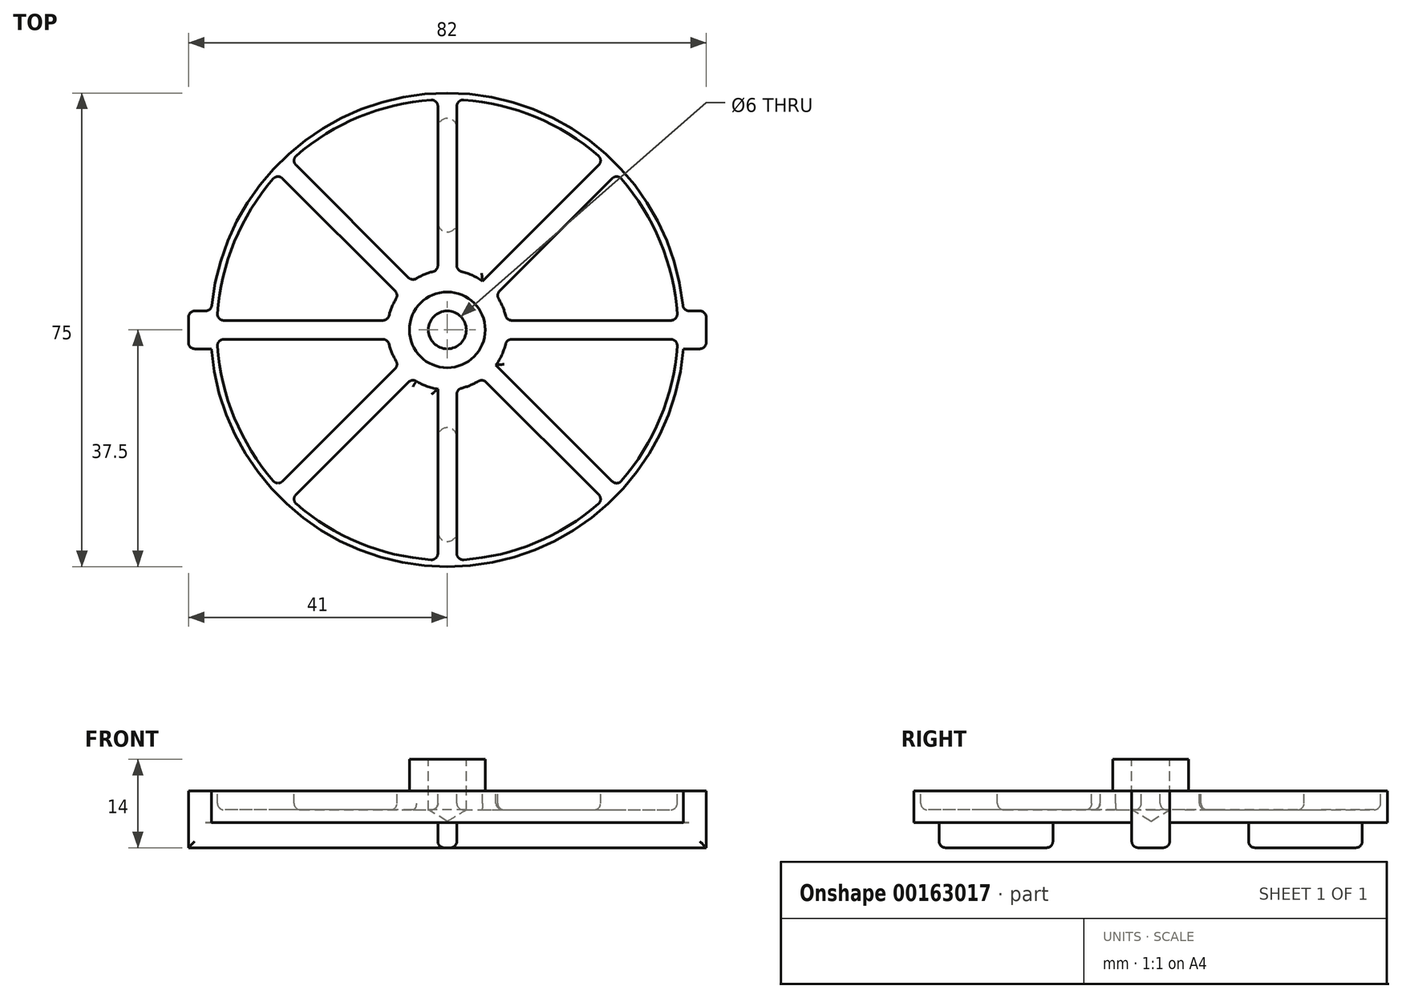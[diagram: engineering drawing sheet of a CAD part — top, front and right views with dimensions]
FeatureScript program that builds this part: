
annotation { "Feature Type Name" : "Feature", "Feature Type Description" : "" }
export const myFeature = defineFeature(function(context is Context, id is Id, definition is map)
    precondition{}
    {
        {
            var Q0;
            Q0=qCreatedBy(makeId("Top.planeOp"),FACE);
            var sketch = newSketch(context, id + "F0", { "sketchPlane" : qUnion([Q0])});
            skCircle(sketch, "E0", {"center": v(0, 0) * mm, "radius": 37.5 * mm});
            skSolve(sketch);
        }
        {
            var Q0;
            Q0 = qSketchRegion(id + "F0", true);
            extrude(context, id + "F1", {"entities" : qUnion([Q0]), "depth" : 5 * mm});
        }
        {
            var Q0;
            Q0=makeQuery(id+"F1.opExtrude","CAP_FACE",FACE,{"disambiguationData":[OSD([sQuery(id+"F0.wireOp",EDGE,"E0")])],"isStart":false});
            var sketch = newSketch(context, id + "F2", { "sketchPlane" : qUnion([Q0])});
            skArc(sketch, "E1", {"start": v(-27.56, 23.93) * mm, "mid": v(-33.72, 13.97) * mm, "end": v(-36.4, 2.57) * mm});
            skArc(sketch, "E2", {"start": v(9.23, 2.26) * mm, "mid": v(8.78, 3.64) * mm, "end": v(8.12, 4.92) * mm});
            skLineSegment(sketch, "E3", {"start": v(1.5, 10.2) * mm, "end": v(1.5, 35.41) * mm});
            skLineSegment(sketch, "E4.MirrorCS", {"start": v(-1.5, 10.2) * mm, "end": v(-1.5, 35.41) * mm});
            skLineSegment(sketch, "E5.1.0", {"start": v(-6.15, 8.27) * mm, "end": v(-23.98, 26.1) * mm});
            skLineSegment(sketch, "E5.1.1", {"start": v(-8.27, 6.15) * mm, "end": v(-26.1, 23.98) * mm});
            skLineSegment(sketch, "E5.2.0", {"start": v(-10.2, 1.5) * mm, "end": v(-35.41, 1.5) * mm});
            skLineSegment(sketch, "E5.2.1", {"start": v(-10.2, -1.5) * mm, "end": v(-35.41, -1.5) * mm});
            skLineSegment(sketch, "E5.3.0", {"start": v(-8.27, -6.15) * mm, "end": v(-26.1, -23.98) * mm});
            skLineSegment(sketch, "E5.3.1", {"start": v(-6.15, -8.27) * mm, "end": v(-23.98, -26.1) * mm});
            skLineSegment(sketch, "E5.4.0", {"start": v(-1.5, -9.38) * mm, "end": v(-1.5, -35.41) * mm});
            skLineSegment(sketch, "E5.4.1", {"start": v(1.5, -10.2) * mm, "end": v(1.5, -35.41) * mm});
            skLineSegment(sketch, "E5.5.0", {"start": v(6.15, -8.27) * mm, "end": v(23.98, -26.1) * mm});
            skLineSegment(sketch, "E5.5.1", {"start": v(7.7, -5.57) * mm, "end": v(26.1, -23.98) * mm});
            skLineSegment(sketch, "E5.6.0", {"start": v(10.2, -1.5) * mm, "end": v(35.41, -1.5) * mm});
            skLineSegment(sketch, "E5.6.1", {"start": v(10.2, 1.5) * mm, "end": v(35.41, 1.5) * mm});
            skLineSegment(sketch, "E5.7.0", {"start": v(8.27, 6.15) * mm, "end": v(26.1, 23.98) * mm});
            skLineSegment(sketch, "E5.7.1", {"start": v(5.57, 7.7) * mm, "end": v(23.98, 26.1) * mm});
            skArc(sketch, "E6.trimOffspring", {"start": v(-2.57, 36.4) * mm, "mid": v(-13.97, 33.72) * mm, "end": v(-23.93, 27.56) * mm});
            skArc(sketch, "E7.trimOffspring", {"start": v(23.93, 27.56) * mm, "mid": v(13.97, 33.72) * mm, "end": v(2.57, 36.4) * mm});
            skArc(sketch, "E8.trimOffspring", {"start": v(36.4, 2.57) * mm, "mid": v(33.72, 13.97) * mm, "end": v(27.56, 23.93) * mm});
            skArc(sketch, "E9.trimOffspring", {"start": v(5.57, 7.7) * mm, "mid": v(4, 8.62) * mm, "end": v(2.26, 9.23) * mm});
            skArc(sketch, "E10.trimOffspring", {"start": v(-2.26, 9.23) * mm, "mid": v(-3.64, 8.78) * mm, "end": v(-4.92, 8.12) * mm});
            skArc(sketch, "E11.trimOffspring", {"start": v(-8.12, 4.92) * mm, "mid": v(-8.78, 3.64) * mm, "end": v(-9.23, 2.26) * mm});
            skArc(sketch, "E12.trimOffspring", {"start": v(-9.23, -2.26) * mm, "mid": v(-8.78, -3.64) * mm, "end": v(-8.12, -4.92) * mm});
            skArc(sketch, "E13.trimOffspring", {"start": v(-4.92, -8.12) * mm, "mid": v(-3.27, -8.92) * mm, "end": v(-1.5, -9.38) * mm});
            skArc(sketch, "E14.trimOffspring", {"start": v(2.26, -9.23) * mm, "mid": v(3.64, -8.78) * mm, "end": v(4.92, -8.12) * mm});
            skArc(sketch, "E15.trimOffspring", {"start": v(7.7, -5.57) * mm, "mid": v(8.62, -4) * mm, "end": v(9.23, -2.26) * mm});
            skArc(sketch, "E16.trimOffspring", {"start": v(27.56, -23.93) * mm, "mid": v(33.72, -13.97) * mm, "end": v(36.4, -2.57) * mm});
            skArc(sketch, "E17.trimOffspring", {"start": v(2.57, -36.4) * mm, "mid": v(13.97, -33.72) * mm, "end": v(23.93, -27.56) * mm});
            skArc(sketch, "E18.trimOffspring", {"start": v(-23.93, -27.56) * mm, "mid": v(-13.97, -33.72) * mm, "end": v(-2.57, -36.4) * mm});
            skArc(sketch, "E19.trimOffspring", {"start": v(-36.4, -2.57) * mm, "mid": v(-33.72, -13.97) * mm, "end": v(-27.56, -23.93) * mm});
            skPoint(sketch, "E20.visualSharp", {"position": v(1.5, 36.47) * mm});
            skArc(sketch, "E20.filletArc", {"start": v(2.57, 36.4) * mm, "mid": v(1.82, 36.14) * mm, "end": v(1.5, 35.41) * mm});
            skPoint(sketch, "E21.visualSharp", {"position": v(-1.5, 36.47) * mm});
            skArc(sketch, "E21.filletArc", {"start": v(-1.5, 35.41) * mm, "mid": v(-1.82, 36.14) * mm, "end": v(-2.57, 36.4) * mm});
            skPoint(sketch, "E22.visualSharp", {"position": v(24.73, 26.85) * mm});
            skArc(sketch, "E22.filletArc", {"start": v(23.98, 26.1) * mm, "mid": v(24.27, 26.84) * mm, "end": v(23.93, 27.56) * mm});
            skPoint(sketch, "E23.visualSharp", {"position": v(26.85, 24.73) * mm});
            skArc(sketch, "E23.filletArc", {"start": v(27.56, 23.93) * mm, "mid": v(26.84, 24.27) * mm, "end": v(26.1, 23.98) * mm});
            skPoint(sketch, "E24.visualSharp", {"position": v(-24.73, 26.85) * mm});
            skArc(sketch, "E24.filletArc", {"start": v(-23.93, 27.56) * mm, "mid": v(-24.27, 26.84) * mm, "end": v(-23.98, 26.1) * mm});
            skPoint(sketch, "E25.visualSharp", {"position": v(-26.85, 24.73) * mm});
            skArc(sketch, "E25.filletArc", {"start": v(-26.1, 23.98) * mm, "mid": v(-26.84, 24.27) * mm, "end": v(-27.56, 23.93) * mm});
            skPoint(sketch, "E26.visualSharp", {"position": v(-36.47, 1.5) * mm});
            skArc(sketch, "E26.filletArc", {"start": v(-36.4, 2.57) * mm, "mid": v(-36.14, 1.82) * mm, "end": v(-35.41, 1.5) * mm});
            skPoint(sketch, "E27.visualSharp", {"position": v(-36.47, -1.5) * mm});
            skArc(sketch, "E27.filletArc", {"start": v(-35.41, -1.5) * mm, "mid": v(-36.14, -1.82) * mm, "end": v(-36.4, -2.57) * mm});
            skPoint(sketch, "E28.visualSharp", {"position": v(36.47, 1.5) * mm});
            skArc(sketch, "E28.filletArc", {"start": v(35.41, 1.5) * mm, "mid": v(36.14, 1.82) * mm, "end": v(36.4, 2.57) * mm});
            skPoint(sketch, "E29.visualSharp", {"position": v(36.47, -1.5) * mm});
            skArc(sketch, "E29.filletArc", {"start": v(36.4, -2.57) * mm, "mid": v(36.14, -1.82) * mm, "end": v(35.41, -1.5) * mm});
            skPoint(sketch, "E30.visualSharp", {"position": v(26.85, -24.73) * mm});
            skArc(sketch, "E30.filletArc", {"start": v(26.1, -23.98) * mm, "mid": v(26.84, -24.27) * mm, "end": v(27.56, -23.93) * mm});
            skPoint(sketch, "E31.visualSharp", {"position": v(24.73, -26.85) * mm});
            skArc(sketch, "E31.filletArc", {"start": v(23.93, -27.56) * mm, "mid": v(24.27, -26.84) * mm, "end": v(23.98, -26.1) * mm});
            skPoint(sketch, "E32.visualSharp", {"position": v(1.5, -36.47) * mm});
            skArc(sketch, "E32.filletArc", {"start": v(1.5, -35.41) * mm, "mid": v(1.82, -36.14) * mm, "end": v(2.57, -36.4) * mm});
            skPoint(sketch, "E33.visualSharp", {"position": v(-1.5, -36.47) * mm});
            skArc(sketch, "E33.filletArc", {"start": v(-2.57, -36.4) * mm, "mid": v(-1.82, -36.14) * mm, "end": v(-1.5, -35.41) * mm});
            skPoint(sketch, "E34.visualSharp", {"position": v(-24.73, -26.85) * mm});
            skArc(sketch, "E34.filletArc", {"start": v(-23.98, -26.1) * mm, "mid": v(-24.27, -26.84) * mm, "end": v(-23.93, -27.56) * mm});
            skPoint(sketch, "E35.visualSharp", {"position": v(-26.85, -24.73) * mm});
            skArc(sketch, "E35.filletArc", {"start": v(-27.56, -23.93) * mm, "mid": v(-26.84, -24.27) * mm, "end": v(-26.1, -23.98) * mm});
            skPoint(sketch, "E36.visualSharp", {"position": v(-1.5, 9.38) * mm});
            skArc(sketch, "E36.filletArc", {"start": v(-2.26, 9.23) * mm, "mid": v(-1.71, 9.58) * mm, "end": v(-1.5, 10.2) * mm});
            skPoint(sketch, "E37.visualSharp", {"position": v(-5.57, 7.7) * mm});
            skArc(sketch, "E37.filletArc", {"start": v(-6.15, 8.27) * mm, "mid": v(-5.56, 7.99) * mm, "end": v(-4.92, 8.12) * mm});
            skPoint(sketch, "E38.visualSharp", {"position": v(-7.7, 5.57) * mm});
            skArc(sketch, "E38.filletArc", {"start": v(-8.12, 4.92) * mm, "mid": v(-7.99, 5.56) * mm, "end": v(-8.27, 6.15) * mm});
            skPoint(sketch, "E39.visualSharp", {"position": v(-9.38, -1.5) * mm});
            skArc(sketch, "E39.filletArc", {"start": v(-9.23, -2.26) * mm, "mid": v(-9.58, -1.71) * mm, "end": v(-10.2, -1.5) * mm});
            skPoint(sketch, "E40.visualSharp", {"position": v(-7.7, -5.57) * mm});
            skArc(sketch, "E40.filletArc", {"start": v(-8.27, -6.15) * mm, "mid": v(-7.99, -5.56) * mm, "end": v(-8.12, -4.92) * mm});
            skPoint(sketch, "E41.visualSharp", {"position": v(-9.38, 1.5) * mm});
            skArc(sketch, "E41.filletArc", {"start": v(-10.2, 1.5) * mm, "mid": v(-9.58, 1.71) * mm, "end": v(-9.23, 2.26) * mm});
            skPoint(sketch, "E42.visualSharp", {"position": v(-5.57, -7.7) * mm});
            skArc(sketch, "E42.filletArc", {"start": v(-4.92, -8.12) * mm, "mid": v(-5.56, -7.99) * mm, "end": v(-6.15, -8.27) * mm});
            skPoint(sketch, "E43.visualSharp", {"position": v(1.5, -9.38) * mm});
            skArc(sketch, "E43.filletArc", {"start": v(2.26, -9.23) * mm, "mid": v(1.71, -9.58) * mm, "end": v(1.5, -10.2) * mm});
            skPoint(sketch, "E44.visualSharp", {"position": v(5.57, -7.7) * mm});
            skArc(sketch, "E44.filletArc", {"start": v(6.15, -8.27) * mm, "mid": v(5.56, -7.99) * mm, "end": v(4.92, -8.12) * mm});
            skPoint(sketch, "E45.visualSharp", {"position": v(9.38, -1.5) * mm});
            skArc(sketch, "E45.filletArc", {"start": v(10.2, -1.5) * mm, "mid": v(9.58, -1.71) * mm, "end": v(9.23, -2.26) * mm});
            skPoint(sketch, "E46.visualSharp", {"position": v(9.38, 1.5) * mm});
            skArc(sketch, "E46.filletArc", {"start": v(9.23, 2.26) * mm, "mid": v(9.58, 1.71) * mm, "end": v(10.2, 1.5) * mm});
            skPoint(sketch, "E47.visualSharp", {"position": v(7.7, 5.57) * mm});
            skArc(sketch, "E47.filletArc", {"start": v(8.27, 6.15) * mm, "mid": v(7.99, 5.56) * mm, "end": v(8.12, 4.92) * mm});
            skPoint(sketch, "E48.visualSharp", {"position": v(1.5, 9.38) * mm});
            skArc(sketch, "E48.filletArc", {"start": v(1.5, 10.2) * mm, "mid": v(1.71, 9.58) * mm, "end": v(2.26, 9.23) * mm});
            skSolve(sketch);
        }
        {
            var Q0;
            Q0 = qSketchRegion(id + "F2", true);
            extrude(context, id + "F3", {"entities" : qUnion([Q0]), "operationType" : NewBodyOperationType.REMOVE, "oppositeDirection" : true, "depth" : 3 * mm});
        }
        {
            var Q0;
            Q0=makeQuery(id+"F1.opExtrude","CAP_FACE",FACE,{"disambiguationData":[OSD([sQuery(id+"F0.wireOp",EDGE,"E0")])],"isStart":true});
            var sketch = newSketch(context, id + "F4", { "sketchPlane" : qUnion([Q0])});
            skLineSegment(sketch, "E49.bottom", {"start": v(41, 3) * mm, "end": v(-41, 3) * mm});
            skLineSegment(sketch, "E49.top", {"start": v(41, -3) * mm, "end": v(-41, -3) * mm});
            skLineSegment(sketch, "E49.left", {"start": v(41, 3) * mm, "end": v(41, -3) * mm});
            skLineSegment(sketch, "E49.right", {"start": v(-41, 3) * mm, "end": v(-41, -3) * mm});
            skPoint(sketch, "E49.middle", {"position": v(0, 0) * mm});
            skSolve(sketch);
        }
        {
            var Q0;
            Q0 = qSketchRegion(id + "F4", true);
            extrude(context, id + "F5", {"entities" : qUnion([Q0]), "operationType" : NewBodyOperationType.ADD, "depth" : 4 * mm});
        }
        {
            var Q0;
            {var subQ0=sQuery(id+"F4.wireOp",EDGE,"E49.top");var subQ1=sQuery(id+"F4.wireOp",EDGE,"E49.bottom");var subQ3=sQuery(id+"F4.wireOp",EDGE,"E49.right");Q0=makeQuery(id+"F5.boolean.opBoolean","SPLIT",FACE,{"disambiguationData":[TD([makeQuery(id+"F5.opExtrude","SWEPT_FACE",FACE,{"disambiguationData":[OSD([subQ3])]})])],"derivedFrom":makeQuery(id+"F5.opExtrude","CAP_FACE",FACE,{"disambiguationData":[OSD([subQ1,subQ0,sQuery(id+"F4.wireOp",EDGE,"E49.left"),subQ3])],"isStart":true})});}
            var sketch = newSketch(context, id + "F6", { "sketchPlane" : qUnion([Q0])});
            skLineSegment(sketch, "E50", {"start": v(-41, 3) * mm, "end": v(-41, -3) * mm});
            skLineSegment(sketch, "E51", {"start": v(-41, -3) * mm, "end": v(-37.38, -3) * mm});
            skArc(sketch, "E52", {"start": v(-37.38, 3) * mm, "mid": v(-37.48, 0) * mm, "end": v(-37.38, -3) * mm});
            skLineSegment(sketch, "E53", {"start": v(-37.38, 3) * mm, "end": v(-41, 3) * mm});
            skLineSegment(sketch, "E54", {"start": v(0, -3.25) * mm, "end": v(0, 3.49) * mm, "construction": true});
            skLineSegment(sketch, "E55.MirrorCS", {"start": v(41, -3) * mm, "end": v(37.38, -3) * mm});
            skLineSegment(sketch, "E56.MirrorCS", {"start": v(41, 3) * mm, "end": v(41, -3) * mm});
            skLineSegment(sketch, "E57.MirrorCS", {"start": v(37.38, 3) * mm, "end": v(41, 3) * mm});
            skArc(sketch, "E58.MirrorCS", {"start": v(37.38, 3) * mm, "mid": v(37.48, 0) * mm, "end": v(37.38, -3) * mm});
            skSolve(sketch);
        }
        {
            var Q0;
            Q0 = qSketchRegion(id + "F6", true);
            var Q1;
            Q1=makeQuery(id+"F1.opExtrude","CAP_FACE",FACE,{"disambiguationData":[OSD([sQuery(id+"F0.wireOp",EDGE,"E0")])],"isStart":false});
            extrude(context, id + "F7", {"entities" : qUnion([Q0]), "operationType" : NewBodyOperationType.ADD, "endBound" : BoundingType.UP_TO_SURFACE, "endBoundEntityFace" : qUnion([Q1]), "depth" : 25 * mm});
        }
        {
            var Q0;
            Q0=makeQuery(id+"F7.boolean.opBoolean","MERGE",EDGE,{"derivedFrom":[makeQuery(id+"F5.opExtrude","SWEPT_EDGE",EDGE,{"disambiguationData":[OSD([sQuery(id+"F4.wireOp",EDGE,"E49.top"),sQuery(id+"F4.wireOp",EDGE,"E49.right")])]}),makeQuery(id+"F7.opExtrude","SWEPT_EDGE",EDGE,{"disambiguationData":[OSD([sQuery(id+"F6.wireOp",EDGE,"E50"),sQuery(id+"F6.wireOp",EDGE,"E53")])]})]});
            var Q1;
            Q1=makeQuery(id+"F7.boolean.opBoolean","MERGE",EDGE,{"derivedFrom":[makeQuery(id+"F5.opExtrude","SWEPT_EDGE",EDGE,{"disambiguationData":[OSD([sQuery(id+"F4.wireOp",EDGE,"E49.bottom"),sQuery(id+"F4.wireOp",EDGE,"E49.right")])]}),makeQuery(id+"F7.opExtrude","SWEPT_EDGE",EDGE,{"disambiguationData":[OSD([sQuery(id+"F6.wireOp",EDGE,"E50"),sQuery(id+"F6.wireOp",EDGE,"E51")])]})]});
            var Q2;
            Q2=makeQuery(id+"F7.boolean.opBoolean","MERGE",EDGE,{"derivedFrom":[makeQuery(id+"F5.opExtrude","SWEPT_EDGE",EDGE,{"disambiguationData":[OSD([sQuery(id+"F4.wireOp",EDGE,"E49.bottom"),sQuery(id+"F4.wireOp",EDGE,"E49.left")])]}),makeQuery(id+"F7.opExtrude","SWEPT_EDGE",EDGE,{"disambiguationData":[OSD([sQuery(id+"F6.wireOp",EDGE,"E55.MirrorCS"),sQuery(id+"F6.wireOp",EDGE,"E56.MirrorCS")])]})]});
            var Q3;
            Q3=makeQuery(id+"F7.boolean.opBoolean","MERGE",EDGE,{"derivedFrom":[makeQuery(id+"F5.opExtrude","SWEPT_EDGE",EDGE,{"disambiguationData":[OSD([sQuery(id+"F4.wireOp",EDGE,"E49.top"),sQuery(id+"F4.wireOp",EDGE,"E49.left")])]}),makeQuery(id+"F7.opExtrude","SWEPT_EDGE",EDGE,{"disambiguationData":[OSD([sQuery(id+"F6.wireOp",EDGE,"E56.MirrorCS"),sQuery(id+"F6.wireOp",EDGE,"E57.MirrorCS")])]})]});
            var Q4;
            Q4=makeQuery(id+"F5.opExtrude","CAP_EDGE",EDGE,{"disambiguationData":[OSD([sQuery(id+"F4.wireOp",EDGE,"E49.top")])],"isStart":false});
            var Q5;
            Q5=makeQuery(id+"F5.opExtrude","CAP_EDGE",EDGE,{"disambiguationData":[OSD([sQuery(id+"F4.wireOp",EDGE,"E49.bottom")])],"isStart":false});
            var Q6;
            {var subQ0=sQuery(id+"F0.wireOp",EDGE,"E0");var subQ1=sQuery(id+"F4.wireOp",EDGE,"E49.top");Q6=makeQuery(id+"F5.boolean.opBoolean","SPLIT",EDGE,{"disambiguationData":[TD([makeQuery(id+"F1.opExtrude","SWEPT_FACE",FACE,{"disambiguationData":[OSD([subQ0])]}),makeQuery(id+"F1.opExtrude","CAP_FACE",FACE,{"disambiguationData":[OSD([subQ0])],"isStart":true}),makeQuery(id+"F5.opExtrude","CAP_FACE",FACE,{"disambiguationData":[OSD([sQuery(id+"F4.wireOp",EDGE,"E49.bottom"),subQ1,sQuery(id+"F4.wireOp",EDGE,"E49.left"),sQuery(id+"F4.wireOp",EDGE,"E49.right")])],"isStart":true}),makeQuery(id+"F5.opExtrude","SWEPT_FACE",FACE,{"disambiguationData":[OSD([subQ1])]})])],"derivedFrom":makeQuery(id+"F5.opExtrude","CAP_EDGE",EDGE,{"disambiguationData":[OSD([subQ1])],"isStart":true})});}
            var Q7;
            {var subQ0=sQuery(id+"F0.wireOp",EDGE,"E0");var subQ1=sQuery(id+"F4.wireOp",EDGE,"E49.bottom");Q7=makeQuery(id+"F5.boolean.opBoolean","SPLIT",EDGE,{"disambiguationData":[TD([makeQuery(id+"F1.opExtrude","SWEPT_FACE",FACE,{"disambiguationData":[OSD([subQ0])]}),makeQuery(id+"F1.opExtrude","CAP_FACE",FACE,{"disambiguationData":[OSD([subQ0])],"isStart":true}),makeQuery(id+"F5.opExtrude","SWEPT_FACE",FACE,{"disambiguationData":[OSD([subQ1])]}),makeQuery(id+"F5.opExtrude","CAP_FACE",FACE,{"disambiguationData":[OSD([subQ1,sQuery(id+"F4.wireOp",EDGE,"E49.top"),sQuery(id+"F4.wireOp",EDGE,"E49.left"),sQuery(id+"F4.wireOp",EDGE,"E49.right")])],"isStart":true})])],"derivedFrom":makeQuery(id+"F5.opExtrude","CAP_EDGE",EDGE,{"disambiguationData":[OSD([subQ1])],"isStart":true})});}
            var Q8;
            Q8=makeQuery(id+"F7.opExtrude","SWEPT_EDGE",EDGE,{"disambiguationData":[OSD([sQuery(id+"F0.wireOp",EDGE,"E0"),sQuery(id+"F6.wireOp",EDGE,"E51"),sQuery(id+"F6.wireOp",EDGE,"E52")])]});
            var Q9;
            Q9=makeQuery(id+"F7.opExtrude","SWEPT_EDGE",EDGE,{"disambiguationData":[OSD([sQuery(id+"F0.wireOp",EDGE,"E0"),sQuery(id+"F6.wireOp",EDGE,"E52"),sQuery(id+"F6.wireOp",EDGE,"E53")])]});
            var Q10;
            Q10=makeQuery(id+"F7.opExtrude","SWEPT_EDGE",EDGE,{"disambiguationData":[OSD([sQuery(id+"F6.wireOp",EDGE,"E57.MirrorCS"),sQuery(id+"F6.wireOp",EDGE,"E58.MirrorCS")])]});
            var Q11;
            Q11=makeQuery(id+"F7.opExtrude","SWEPT_EDGE",EDGE,{"disambiguationData":[OSD([sQuery(id+"F6.wireOp",EDGE,"E55.MirrorCS"),sQuery(id+"F6.wireOp",EDGE,"E58.MirrorCS")])]});
            fillet(context, id + "F8", {"entities" : qUnion([Q0, Q1, Q2, Q3, Q4, Q5, Q6, Q7, Q8, Q9, Q10, Q11]), "radius" : 1 * mm, "tangentPropagation" : true, "allowEdgeOverflow" : false});
        }
        {
            var Q0;
            {var subQ0=sQuery(id+"F0.wireOp",EDGE,"E0");var subQ1=sQuery(id+"F4.wireOp",EDGE,"E49.bottom");Q0=makeQuery(id+"F5.boolean.opBoolean","SPLIT",FACE,{"disambiguationData":[TD([makeQuery(id+"F5.opExtrude","SWEPT_FACE",FACE,{"disambiguationData":[OSD([subQ1])]})])],"derivedFrom":makeQuery(id+"F1.opExtrude","CAP_FACE",FACE,{"disambiguationData":[OSD([subQ0])],"isStart":true})});}
            var sketch = newSketch(context, id + "F9", { "sketchPlane" : qUnion([Q0])});
            skPoint(sketch, "E59.startSnap0", {"position": v(0, 37.5) * mm});
            skLineSegment(sketch, "E60", {"start": v(0, 0) * mm, "end": v(5.23, 0) * mm, "construction": true});
            skArc(sketch, "E61.0.startCap", {"start": v(-1.5, 32) * mm, "mid": v(0, 33.5) * mm, "end": v(1.5, 32) * mm});
            skArc(sketch, "E61.0.endCap", {"start": v(1.5, 17) * mm, "mid": v(0, 15.5) * mm, "end": v(-1.5, 17) * mm});
            skLineSegment(sketch, "E61.0.left", {"start": v(1.5, 32) * mm, "end": v(1.5, 17) * mm});
            skLineSegment(sketch, "E61.0.right", {"start": v(-1.5, 32) * mm, "end": v(-1.5, 17) * mm});
            skArc(sketch, "E62.MirrorCS", {"start": v(-1.5, -32) * mm, "mid": v(0, -33.5) * mm, "end": v(1.5, -32) * mm});
            skLineSegment(sketch, "E63.MirrorCS", {"start": v(1.5, -32) * mm, "end": v(1.5, -17) * mm});
            skLineSegment(sketch, "E64.MirrorCS", {"start": v(-1.5, -32) * mm, "end": v(-1.5, -17) * mm});
            skArc(sketch, "E65.MirrorCS", {"start": v(1.5, -17) * mm, "mid": v(0, -15.5) * mm, "end": v(-1.5, -17) * mm});
            skSolve(sketch);
        }
        {
            var Q0;
            Q0 = qSketchRegion(id + "F9", true);
            extrude(context, id + "F10", {"entities" : qUnion([Q0]), "operationType" : NewBodyOperationType.ADD, "depth" : 4 * mm});
        }
        {
            var Q0;
            Q0=makeQuery(id+"F10.opExtrude","CAP_EDGE",EDGE,{"disambiguationData":[OSD([sQuery(id+"F9.wireOp",EDGE,"E61.0.left")])],"isStart":false});
            var Q1;
            Q1=makeQuery(id+"F10.opExtrude","CAP_EDGE",EDGE,{"disambiguationData":[OSD([sQuery(id+"F9.wireOp",EDGE,"E61.0.right")])],"isStart":false});
            var Q2;
            Q2=makeQuery(id+"F10.opExtrude","CAP_FACE",FACE,{"disambiguationData":[OSD([sQuery(id+"F9.wireOp",EDGE,"E62.MirrorCS"),sQuery(id+"F9.wireOp",EDGE,"E63.MirrorCS"),sQuery(id+"F9.wireOp",EDGE,"E64.MirrorCS"),sQuery(id+"F9.wireOp",EDGE,"E65.MirrorCS")])],"isStart":false});
            var Q3;
            Q3=makeQuery(id+"F10.opExtrude","CAP_EDGE",EDGE,{"disambiguationData":[OSD([sQuery(id+"F9.wireOp",EDGE,"E63.MirrorCS")])],"isStart":false});
            fillet(context, id + "F11", {"entities" : qUnion([Q0, Q1, Q2, Q3]), "radius" : 1 * mm, "tangentPropagation" : true, "allowEdgeOverflow" : false});
        }
        {
            var Q0;
            {var subQ0=sQuery(id+"F0.wireOp",EDGE,"E0");Q0=makeQuery(id+"F7.boolean.opBoolean","MERGE",FACE,{"derivedFrom":[makeQuery(id+"F1.opExtrude","CAP_FACE",FACE,{"disambiguationData":[OSD([subQ0])],"isStart":false}),makeQuery(id+"F7.opExtrude","CAP_FACE",FACE,{"disambiguationData":[OSD([subQ0]),ownerDisambiguation([makeQuery(id+"F7.opExtrude","SWEPT_BODY",BODY,{"disambiguationData":[OSD([sQuery(id+"F6.wireOp",EDGE,"E50"),sQuery(id+"F6.wireOp",EDGE,"E51"),sQuery(id+"F6.wireOp",EDGE,"E52"),sQuery(id+"F6.wireOp",EDGE,"E53")])]})])],"isStart":false}),makeQuery(id+"F7.opExtrude","CAP_FACE",FACE,{"disambiguationData":[OSD([subQ0]),ownerDisambiguation([makeQuery(id+"F7.opExtrude","SWEPT_BODY",BODY,{"disambiguationData":[OSD([sQuery(id+"F6.wireOp",EDGE,"E55.MirrorCS"),sQuery(id+"F6.wireOp",EDGE,"E56.MirrorCS"),sQuery(id+"F6.wireOp",EDGE,"E57.MirrorCS"),sQuery(id+"F6.wireOp",EDGE,"E58.MirrorCS")])]})])],"isStart":false})]});}
            var sketch = newSketch(context, id + "F12", { "sketchPlane" : qUnion([Q0])});
            skCircle(sketch, "E66", {"center": v(0, 0) * mm, "radius": 6 * mm});
            skSolve(sketch);
        }
        {
            var Q0;
            Q0 = qSketchRegion(id + "F12", true);
            extrude(context, id + "F13", {"entities" : qUnion([Q0]), "operationType" : NewBodyOperationType.ADD, "depth" : 5 * mm});
        }
        {
            var Q0;
            Q0=makeQuery(id+"F13.opExtrude","CAP_FACE",FACE,{"disambiguationData":[OSD([sQuery(id+"F12.wireOp",EDGE,"E66")])],"isStart":false});
            var sketch = newSketch(context, id + "F14", { "sketchPlane" : qUnion([Q0])});
            skPoint(sketch, "E67", {"position": v(0, 0) * mm});
            skSolve(sketch);
        }
        {
            var Q0;
            Q0=sQuery(id+"F14.wireOp",VERTEX,"E67");
            var Q1;
            Q1=makeQuery(id+"F1.opExtrude","SWEPT_BODY",BODY,{"disambiguationData":[OSD([sQuery(id+"F0.wireOp",EDGE,"E0")])]});
            hole(context, id + "F15", {"style" : HoleStyle.SIMPLE, "endStyle" : HoleEndStyle.BLIND, "holeDiameter" : 6 * mm, "holeDepth" : 8 * mm, "locations" : qUnion([Q0]), "scope" : qUnion([Q1])});
        }
        {
            var Q0;
            Q0=makeQuery(id+"F3.boolean.opBoolean","COPY",EDGE,{"derivedFrom":makeQuery(id+"F3.opExtrude","CAP_EDGE",EDGE,{"disambiguationData":[OSD([sQuery(id+"F2.wireOp",EDGE,"E5.2.1")])],"isStart":false})});
            var Q1;
            Q1=makeQuery(id+"F3.boolean.opBoolean","COPY",EDGE,{"derivedFrom":makeQuery(id+"F3.opExtrude","CAP_EDGE",EDGE,{"disambiguationData":[OSD([sQuery(id+"F2.wireOp",EDGE,"E1")])],"isStart":false})});
            var Q2;
            Q2=makeQuery(id+"F3.boolean.opBoolean","COPY",EDGE,{"derivedFrom":makeQuery(id+"F3.opExtrude","CAP_EDGE",EDGE,{"disambiguationData":[OSD([sQuery(id+"F2.wireOp",EDGE,"E6.trimOffspring")])],"isStart":false})});
            var Q3;
            Q3=makeQuery(id+"F3.boolean.opBoolean","COPY",EDGE,{"derivedFrom":makeQuery(id+"F3.opExtrude","CAP_EDGE",EDGE,{"disambiguationData":[OSD([sQuery(id+"F2.wireOp",EDGE,"E3")])],"isStart":false})});
            var Q4;
            Q4=makeQuery(id+"F3.boolean.opBoolean","COPY",EDGE,{"derivedFrom":makeQuery(id+"F3.opExtrude","CAP_EDGE",EDGE,{"disambiguationData":[OSD([sQuery(id+"F2.wireOp",EDGE,"E5.7.0")])],"isStart":false})});
            var Q5;
            Q5=makeQuery(id+"F3.boolean.opBoolean","COPY",EDGE,{"derivedFrom":makeQuery(id+"F3.opExtrude","CAP_EDGE",EDGE,{"disambiguationData":[OSD([sQuery(id+"F2.wireOp",EDGE,"E7.trimOffspring")])],"isStart":false})});
            var Q6;
            Q6=makeQuery(id+"F3.boolean.opBoolean","COPY",EDGE,{"derivedFrom":makeQuery(id+"F3.opExtrude","CAP_EDGE",EDGE,{"disambiguationData":[OSD([sQuery(id+"F2.wireOp",EDGE,"E20.filletArc")])],"isStart":false})});
            var Q7;
            Q7=makeQuery(id+"F3.boolean.opBoolean","COPY",EDGE,{"derivedFrom":makeQuery(id+"F3.opExtrude","CAP_EDGE",EDGE,{"disambiguationData":[OSD([sQuery(id+"F2.wireOp",EDGE,"E5.7.1")])],"isStart":false})});
            var Q8;
            Q8=makeQuery(id+"F3.boolean.opBoolean","COPY",FACE,{"derivedFrom":makeQuery(id+"F3.opExtrude","CAP_FACE",FACE,{"disambiguationData":[OSD([sQuery(id+"F2.wireOp",EDGE,"E5.5.1"),sQuery(id+"F2.wireOp",EDGE,"E5.6.0"),sQuery(id+"F2.wireOp",EDGE,"E15.trimOffspring"),sQuery(id+"F2.wireOp",EDGE,"E16.trimOffspring"),sQuery(id+"F2.wireOp",EDGE,"E29.filletArc"),sQuery(id+"F2.wireOp",EDGE,"E30.filletArc"),sQuery(id+"F2.wireOp",EDGE,"E45.filletArc")])],"isStart":false})});
            var Q9;
            Q9=makeQuery(id+"F3.boolean.opBoolean","COPY",EDGE,{"derivedFrom":makeQuery(id+"F3.opExtrude","CAP_EDGE",EDGE,{"disambiguationData":[OSD([sQuery(id+"F2.wireOp",EDGE,"E5.6.0")])],"isStart":false})});
            var Q10;
            Q10=makeQuery(id+"F3.boolean.opBoolean","COPY",EDGE,{"derivedFrom":makeQuery(id+"F3.opExtrude","CAP_EDGE",EDGE,{"disambiguationData":[OSD([sQuery(id+"F2.wireOp",EDGE,"E5.5.0")])],"isStart":false})});
            var Q11;
            Q11=makeQuery(id+"F3.boolean.opBoolean","COPY",EDGE,{"derivedFrom":makeQuery(id+"F3.opExtrude","CAP_EDGE",EDGE,{"disambiguationData":[OSD([sQuery(id+"F2.wireOp",EDGE,"E5.4.0")])],"isStart":false})});
            fillet(context, id + "F16", {"entities" : qUnion([Q0, Q1, Q2, Q3, Q4, Q5, Q6, Q7, Q8, Q9, Q10, Q11]), "tangentPropagation" : true, "radius" : 1 * mm, "defaultsChanged" : false, "vertexSettings" : [], "allowEdgeOverflow" : false});
        }
    });
